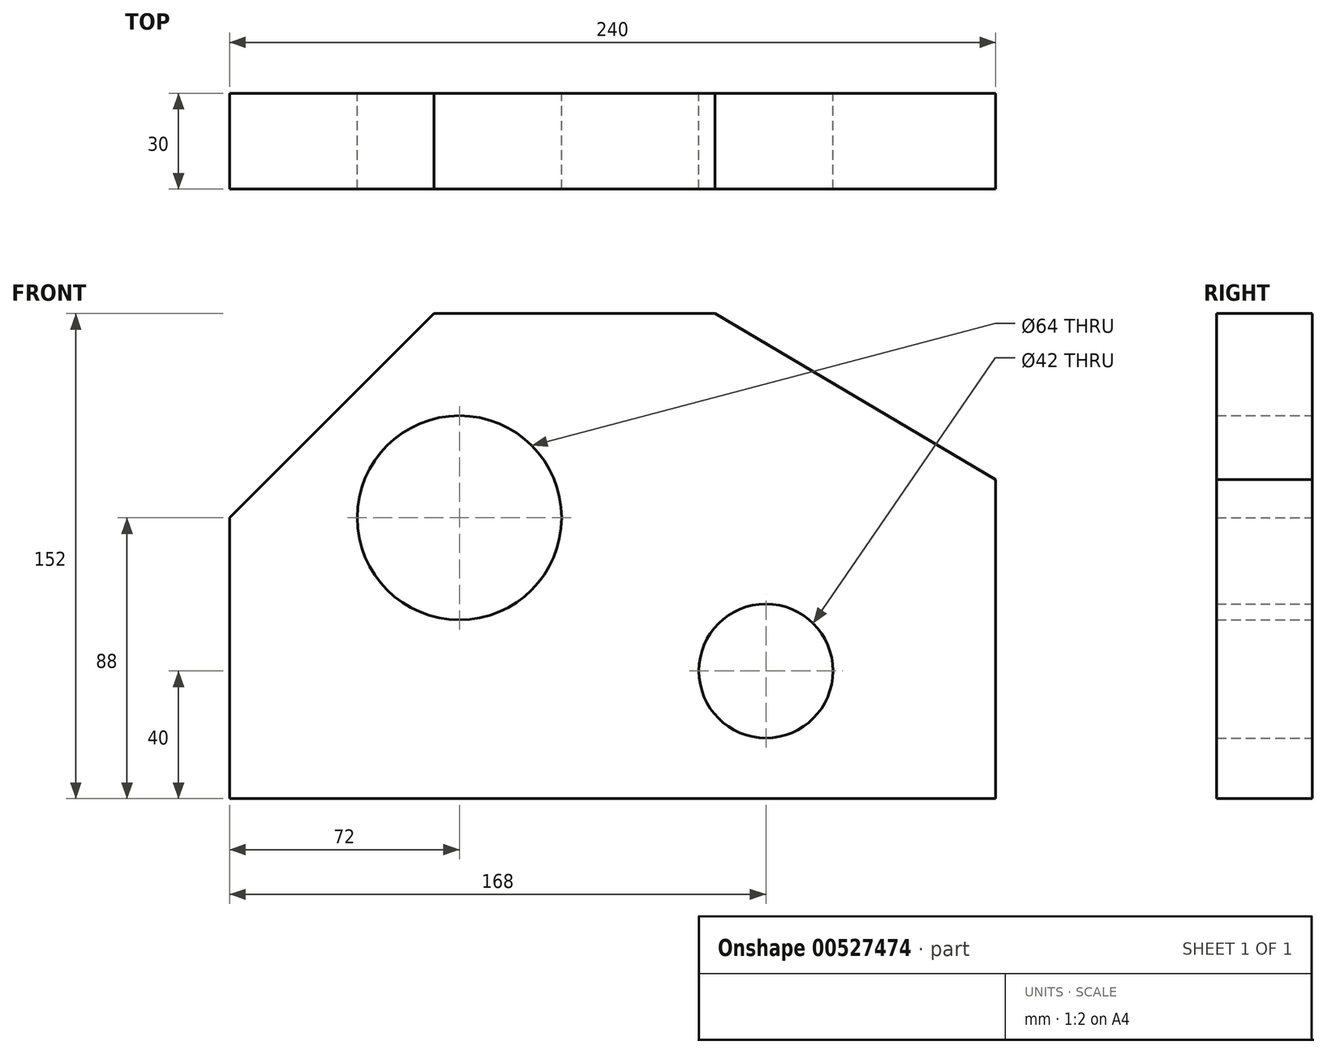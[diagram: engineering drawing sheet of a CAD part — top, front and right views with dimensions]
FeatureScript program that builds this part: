
annotation { "Feature Type Name" : "Feature", "Feature Type Description" : "" }
export const myFeature = defineFeature(function(context is Context, id is Id, definition is map)
    precondition{}
    {
        {
            var Q0;
            Q0=qCreatedBy(makeId("Front.planeOp"),FACE);
            var sketch = newSketch(context, id + "F0", { "sketchPlane" : qUnion([Q0])});
            skLineSegment(sketch, "E0", {"start": v(0, 0) * mm, "end": v(0, -88) * mm});
            skLineSegment(sketch, "E1", {"start": v(0, -88) * mm, "end": v(240, -88) * mm});
            skLineSegment(sketch, "E2", {"start": v(240, -88) * mm, "end": v(240, 12) * mm});
            skLineSegment(sketch, "E3", {"start": v(0, 0) * mm, "end": v(64, 64) * mm});
            skLineSegment(sketch, "E4", {"start": v(64, 64) * mm, "end": v(152, 64) * mm});
            skLineSegment(sketch, "E5", {"start": v(152, 64) * mm, "end": v(240, 12) * mm});
            skCircle(sketch, "E6", {"center": v(72, 0) * mm, "radius": 32 * mm});
            skCircle(sketch, "E7", {"center": v(168, -48) * mm, "radius": 21 * mm});
            skSolve(sketch);
        }
        {
            var Q0;
            Q0 = qSketchRegion(id + "F0", true);
            extrude(context, id + "F1", {"entities" : qUnion([Q0]), "depth" : 30 * mm, "offsetDistance" : 25 * mm});
        }
    });
